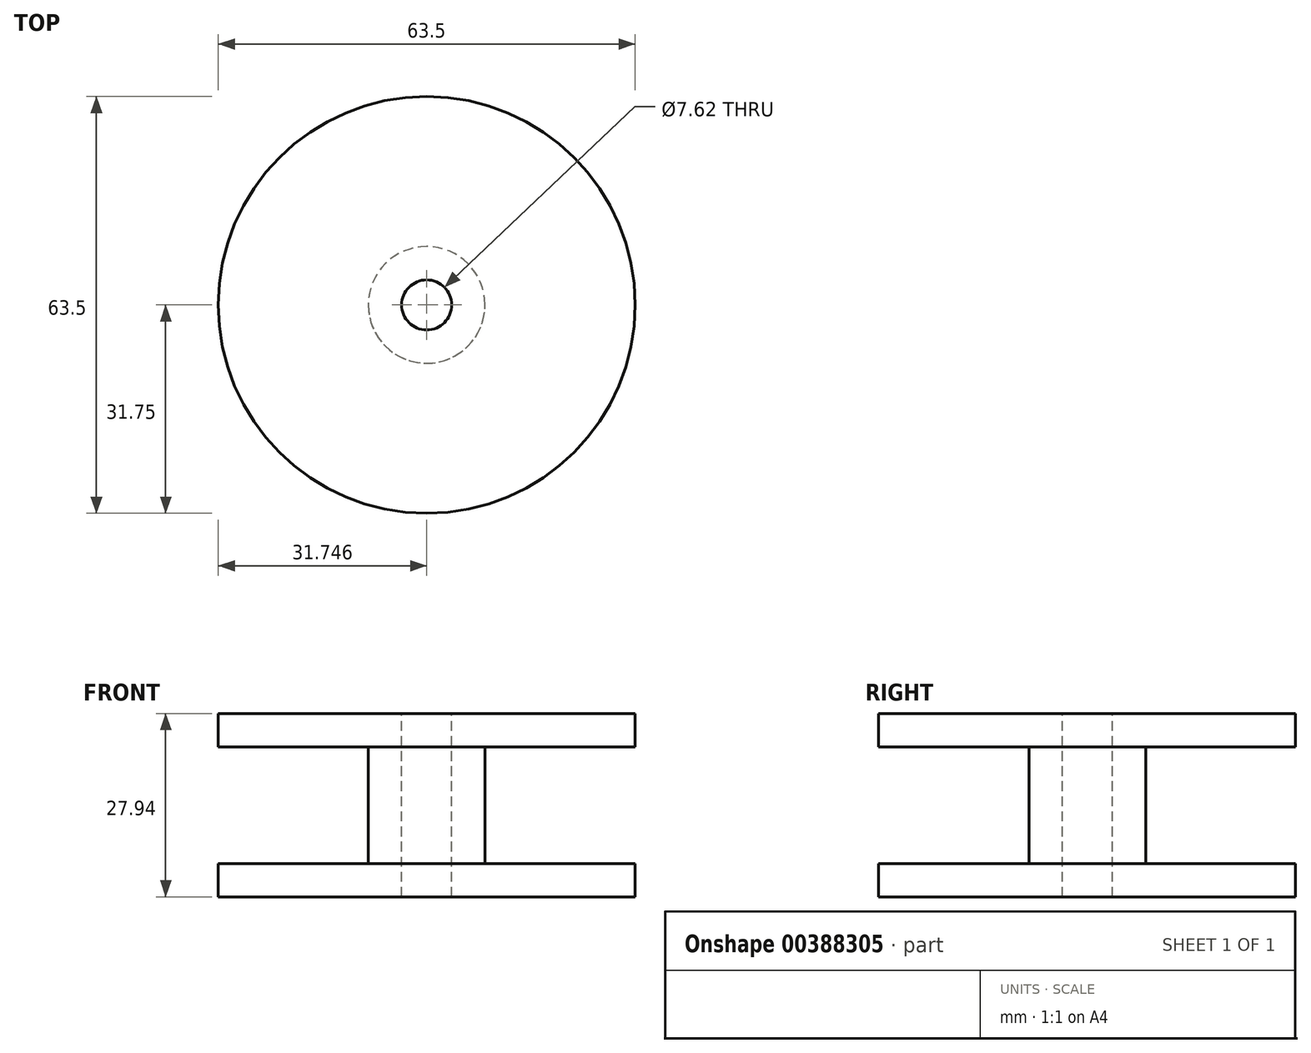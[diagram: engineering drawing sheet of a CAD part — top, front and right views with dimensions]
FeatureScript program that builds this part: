
annotation { "Feature Type Name" : "Feature", "Feature Type Description" : "" }
export const myFeature = defineFeature(function(context is Context, id is Id, definition is map)
    precondition{}
    {
        {
            var Q0;
            Q0=qCreatedBy(makeId("Front.planeOp"),FACE);
            var sketch = newSketch(context, id + "F0", { "sketchPlane" : qUnion([Q0])});
            skLineSegment(sketch, "E0", {"start": v(-16, 31.96) * mm, "end": v(15.76, 31.96) * mm});
            skLineSegment(sketch, "E1", {"start": v(15.76, 31.96) * mm, "end": v(15.76, 4.02) * mm});
            skLineSegment(sketch, "E2", {"start": v(15.76, 4.02) * mm, "end": v(-16, 4.02) * mm});
            skLineSegment(sketch, "E3", {"start": v(-16, 4.02) * mm, "end": v(-16, 31.96) * mm});
            skSolve(sketch);
        }
        {
            var Q0;
            Q0=qSketchRegion(id+"F0",true);
            var Q1;
            Q1=sQuery(id+"F0.wireOp",EDGE,"E1");
            revolve(context, id + "F1", {"entities" : qUnion([Q0]), "axis" : qUnion([Q1]), "revolveType" : RevolveType.FULL});
        }
        {
            var Q0;
            Q0=makeQuery(id+"F1.opRevolve","SWEPT_FACE",FACE,{"disambiguationData":[OSD([sQuery(id+"F0.wireOp",EDGE,"E0")])]});
            var sketch = newSketch(context, id + "F2", { "sketchPlane" : qUnion([Q0])});
            skCircle(sketch, "E4", {"center": v(15.76, 0) * mm, "radius": 3.8 * mm});
            skSolve(sketch);
        }
        {
            var Q0;
            Q0=qSketchRegion(id+"F2",true);
            extrude(context, id + "F3", {"entities" : qUnion([Q0]), "operationType" : NewBodyOperationType.REMOVE, "oppositeDirection" : true, "depth" : 70.2 * mm});
        }
        {
            var Q0;
            Q0=makeQuery(id+"F1.opRevolve","SWEPT_FACE",FACE,{"disambiguationData":[OSD([sQuery(id+"F0.wireOp",EDGE,"E3")])]});
            shell(context, id + "F4", {"entities" : qUnion([Q0]), "thickness" : 5.08 * mm});
        }
    });
